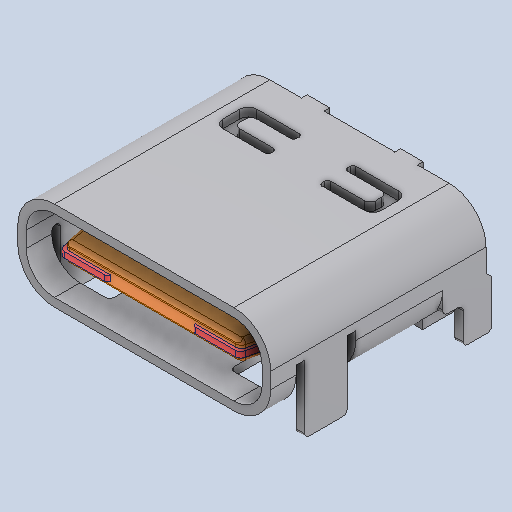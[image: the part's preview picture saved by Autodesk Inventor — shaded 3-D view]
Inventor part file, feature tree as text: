
AUTODESK INVENTOR PART (.ipt)
format: ipt  version: 2024.3 (Build 283343000, 343)  size: 486,400 bytes
history: native  units: in
note: dims shown in document units (in); Inventor stores cm internally (conversion verified against a paired STEP export)
features: other x29, mirror x1
ambient origin geometry x8: Origin, YZ Plane, XZ Plane, XY Plane, X Axis, Y Axis, Z Axis, Center Point
bodies: Solid1 (feature_tree), Solid2 (feature_tree), Solid3 (feature_tree), Solid4 (feature_tree), Solid5 (feature_tree), Solid6 (feature_tree), Solid7 (feature_tree), Solid8 (feature_tree), Solid9 (feature_tree), Solid10 (feature_tree), Solid11 (feature_tree), Solid12 (feature_tree), Solid13 (feature_tree), Solid14 (feature_tree), Solid15 (feature_tree), Solid16 (feature_tree), Solid17 (feature_tree), Solid18 (feature_tree), Solid19 (feature_tree), Solid20 (feature_tree), Solid21 (feature_tree), Solid22 (feature_tree), Solid23 (feature_tree), Solid24 (feature_tree), Solid25 (feature_tree), Solid26 (feature_tree), Solid27 (feature_tree), Solid28 (feature_tree), Solid29 (feature_tree), Solid30 (feature_tree)
feature tree (30):
  mirror  "Mirror1"
  other  "Cut-Extrude5[1]"
  other  "Cut-Extrude5[2]"
  other  "Cut-Extrude5[3]"
  other  "Cut-Extrude5[4]"
  other  "Cut-Extrude5[5]"
  other  "Cut-Extrude5[6]"
  other  "Cut-Extrude5[7]"
  other  "Cut-Extrude5[8]"
  other  "Cut-Extrude5[9]"
  other  "Cut-Extrude5[10]"
  other  "Cut-Extrude5[11]"
  other  "Cut-Extrude5[12]"
  other  "Cut-Extrude5[13]"
  other  "Cut-Extrude5[14]"
  other  "Cut-Extrude6[1]"
  other  "Cut-Extrude6[2]"
  other  "Cut-Extrude6[3]"
  other  "Cut-Extrude6[4]"
  other  "Cut-Extrude6[5]"
  other  "Cut-Extrude6[6]"
  other  "Cut-Extrude6[7]"
  other  "Cut-Extrude6[8]"
  other  "Cut-Extrude6[9]"
  other  "Cut-Extrude6[10]"
  other  "Cut-Extrude6[11]"
  other  "Cut-Extrude6[12]"
  other  "Boss-Extrude8[1]"
  other  "Boss-Extrude8[2]"
  other  "Cut-Extrude10"
